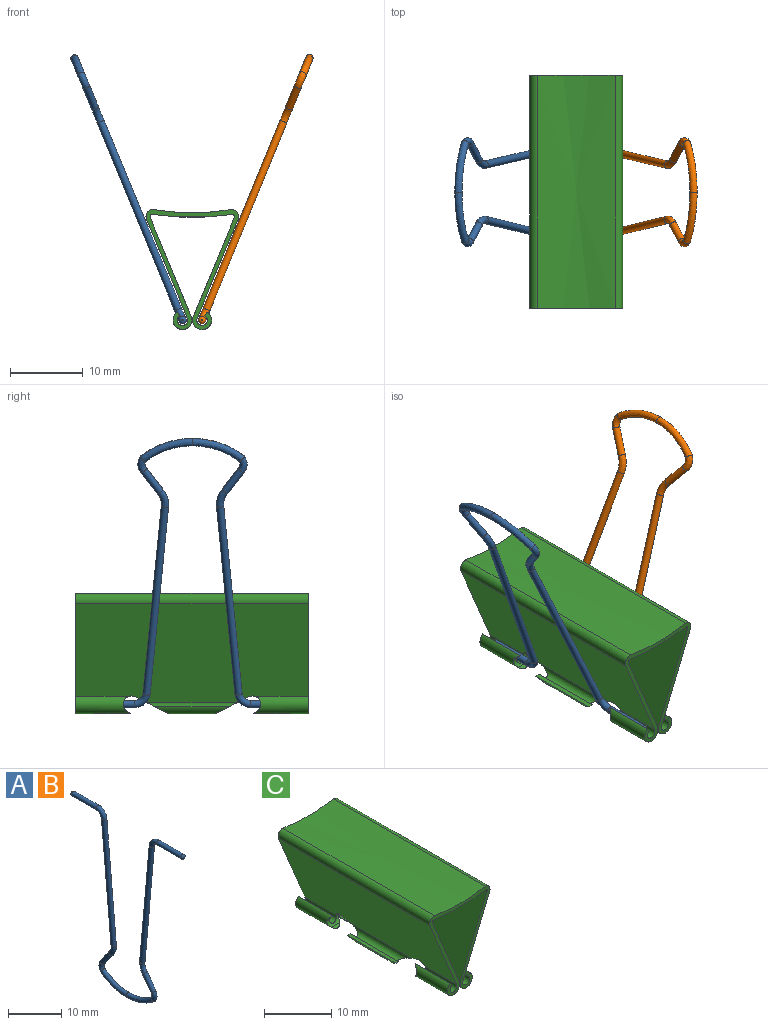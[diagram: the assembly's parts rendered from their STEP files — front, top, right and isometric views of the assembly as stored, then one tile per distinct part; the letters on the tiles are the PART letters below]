
ASSEMBLY  parts=3 mates=2
PART A: 18 faces, bbox 2x29.7x40.1 mm
  f0: plane 0.2x0.2mm, normal (0,1,0), area 0mm2, adj f16
  f1: plane 0.2x0.2mm, normal (0,-1,0), area 0mm2, adj f17
  f2: cylinder r=0.5mm len=27.98mm, axis (0,0.09,1), area 88mm2, adj f3,f5
  f3: torus R=1.71mm, axis (-1,0,0), area 7.9mm2, adj f2,f4
  f4: cylinder r=0.5mm len=6.42mm, axis (0,1,0), area 20.2mm2, adj f3,f16
  f5: bspline ~2.55x1.59mm, area 7.3mm2, adj f2,f7
  f6: bspline ~2.45x2mm, area 5.8mm2, adj f7,f9
  f7: cylinder r=0.5mm len=3.76mm, axis (0,-0.58,0.81), area 12.2mm2, adj f5,f6
  f8: bspline ~7.21x3.45mm, area 23mm2, adj f9,f10
  f9: bspline ~7.21x3.45mm, area 23mm2, adj f6,f8
  f10: bspline ~2.45x2mm, area 5.8mm2, adj f8,f11
  f11: cylinder r=0.5mm len=3.76mm, axis (0,-0.58,-0.81), area 12.2mm2, adj f10,f15
  f12: cylinder r=0.5mm len=6.42mm, axis (0,1,0), area 20.2mm2, adj f13,f17
  f13: torus R=1.71mm, axis (-1,0,0), area 7.9mm2, adj f12,f14
  f14: cylinder r=0.5mm len=27.98mm, axis (0,0.09,-1), area 88mm2, adj f13,f15
  f15: bspline ~2.55x1.59mm, area 7.3mm2, adj f11,f14
  f16: torus R=0.1mm, axis (0,-1,0), area 1.4mm2, adj f0,f4
  f17: torus R=0.1mm, axis (0,-1,0), area 1.4mm2, adj f1,f12
PART B: same geometry as A
PART C: 42 faces, bbox 12.7x32x16.5 mm
  f0: cylinder r=0.72mm len=12.71mm, axis (0,1,0), area 21.9mm2, adj f2,f3,f4,f40
  f1: cylinder r=1.3mm len=13.59mm, axis (0,1,0), area 36.7mm2, adj f2,f3,f8,f40
  f2: plane 4.59x2.55mm, normal (0,0.45,-0.89), area 5mm2, adj f0,f1,f4,f8,f36,f40
  f3: plane 4.59x2.55mm, normal (0,-0.45,-0.89), area 5mm2, adj f0,f1,f4,f8,f38,f40
  f4: plane 32x13.54mm, normal (-0.92,0,-0.38), area 465.4mm2, adj f0,f2,f3,f5,f19,f20,f28,f29
  f5: cylinder r=0.72mm len=6.78mm, axis (0,1,0), area 21.7mm2, adj f4,f6,f28,f38
  f6: plane 7.4x0.48mm, normal (0.84,0,0.54), area 4mm2, adj f5,f7,f28,f38
  f7: cylinder r=1.3mm len=7.53mm, axis (0,1,0), area 40.7mm2, adj f6,f8,f28,f38,f39
  f8: plane 32x13.54mm, normal (0.92,0,0.38), area 466.7mm2, adj f1,f2,f3,f7,f22,f23,f28,f29
  f9: plane 32x13.54mm, normal (-0.92,0,0.38), area 466.7mm2, adj f10,f11,f25,f26,f28,f29,f30,f31
  f10: cylinder r=1.3mm len=7.53mm, axis (0,1,0), area 40.7mm2, adj f9,f12,f28,f33,f35
  f11: cylinder r=1.3mm len=13.59mm, axis (0,1,0), area 36.7mm2, adj f9,f31,f34,f41
  f12: plane 7.4x0.48mm, normal (-0.84,0,0.54), area 4mm2, adj f10,f15,f28,f33
  f13: plane 7.4x0.48mm, normal (-0.84,0,0.54), area 4mm2, adj f26,f27,f29,f30
  f14: cylinder r=0.72mm len=12.71mm, axis (0,1,0), area 21.9mm2, adj f16,f31,f34,f41
  f15: cylinder r=0.72mm len=6.78mm, axis (0,1,0), area 21.7mm2, adj f12,f16,f28,f33
  f16: plane 32x13.54mm, normal (0.92,0,-0.38), area 465.4mm2, adj f14,f15,f17,f27,f28,f29,f30,f31
  f17: cylinder r=1mm len=32mm, axis (0,1,0), area 63.2mm2, adj f16,f18,f28,f29
  f18: extruded ~32x10.71mm, area 344.6mm2, adj f17,f19,f28,f29
  f19: cylinder r=1mm len=32mm, axis (0,1,0), area 63.2mm2, adj f4,f18,f28,f29
  f20: cylinder r=0.72mm len=6.78mm, axis (0,1,0), area 21.7mm2, adj f4,f21,f29,f36
  f21: plane 7.4x0.48mm, normal (0.84,0,0.54), area 4mm2, adj f20,f22,f29,f36
  f22: cylinder r=1.3mm len=7.53mm, axis (0,1,0), area 40.7mm2, adj f8,f21,f29,f36,f37
  f23: cylinder r=0.43mm len=32mm, axis (0,1,0), area 17.6mm2, adj f8,f24,f28,f29
  f24: extruded ~32x11.25mm, area 361.4mm2, adj f23,f25,f28,f29
  f25: cylinder r=0.43mm len=32mm, axis (0,1,0), area 17.6mm2, adj f9,f24,f28,f29
  f26: cylinder r=1.3mm len=7.53mm, axis (0,1,0), area 40.7mm2, adj f9,f13,f29,f30,f32
  f27: cylinder r=0.72mm len=6.78mm, axis (0,1,0), area 21.7mm2, adj f13,f16,f29,f30
  f28: plane 16.49x12.73mm, normal (0,-1,0), area 30.4mm2, adj f4,f5,f6,f7,f8,f9,f10,f12
  f29: plane 16.49x12.73mm, normal (0,1,0), area 30.4mm2, adj f4,f8,f9,f13,f16,f17,f18,f19
  f30: cylinder r=1.14mm len=2.59mm, axis (1,0,0), area 3.9mm2, adj f9,f13,f16,f26,f27,f31,f32
  f31: plane 4.59x2.55mm, normal (0,0.45,-0.89), area 5mm2, adj f9,f11,f14,f16,f30,f41
  f32: plane 1.72x0.48mm, normal (0,-0.56,0.83), area 0.7mm2, adj f26,f30
  f33: cylinder r=1.14mm len=2.59mm, axis (1,0,0), area 3.9mm2, adj f9,f10,f12,f15,f16,f34,f35
  f34: plane 4.59x2.55mm, normal (0,-0.45,-0.89), area 5mm2, adj f9,f11,f14,f16,f33,f41
  f35: plane 1.72x0.48mm, normal (0,0.56,0.83), area 0.7mm2, adj f10,f33
  f36: cylinder r=1.14mm len=2.59mm, axis (1,0,0), area 3.9mm2, adj f2,f4,f8,f20,f21,f22,f37
  f37: plane 1.72x0.48mm, normal (0,-0.56,0.83), area 0.7mm2, adj f22,f36
  f38: cylinder r=1.14mm len=2.59mm, axis (1,0,0), area 3.9mm2, adj f3,f4,f5,f6,f7,f8,f39
  f39: plane 1.72x0.48mm, normal (0,0.56,0.83), area 0.7mm2, adj f7,f38
  f40: plane 10.3x0.61mm, normal (0,0,1), area 6.3mm2, adj f0,f1,f2,f3
  f41: plane 10.3x0.61mm, normal (0,0,1), area 6.3mm2, adj f11,f14,f31,f34
PLACE A rot(axis=(0,1,0),157.6deg) t=(-1.32,-0.14,0.26)mm
PLACE B rot(axis=(0,-1,0),157.7deg) t=(1.38,-0.14,0.26)mm
PLACE C t=(0.03,15.94,0.54)mm fixed
MATE revolute A.f4 <-> C.f0  axis (0,1,0) through (-1.32,-11.36,0.26)mm
MATE revolute B.f4 <-> C.f10  axis (0,1,0) through (1.38,-11.36,0.26)mm
